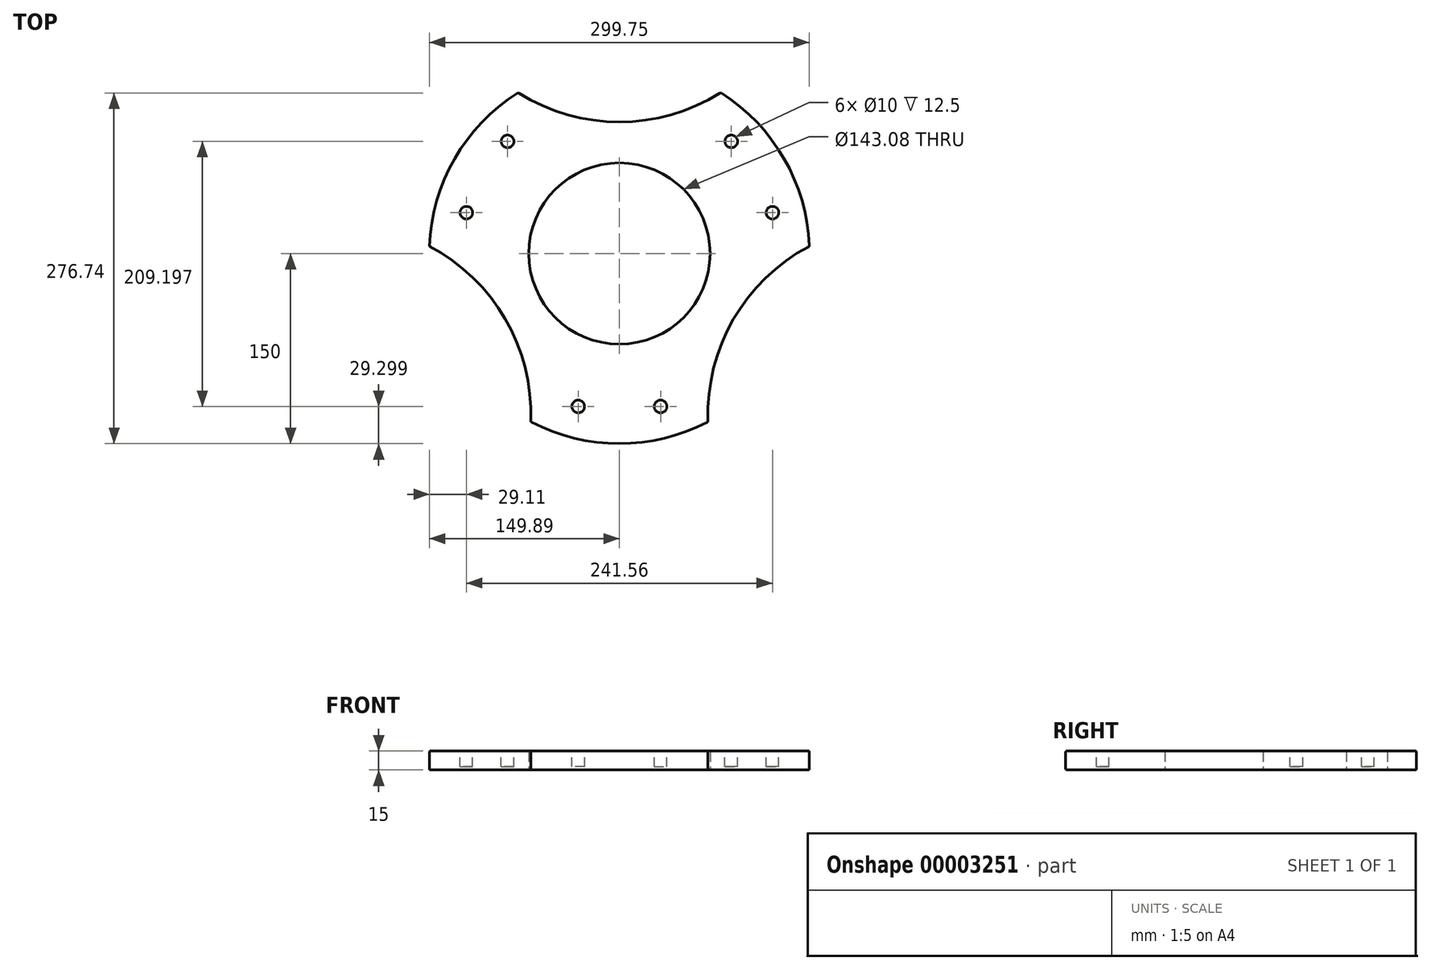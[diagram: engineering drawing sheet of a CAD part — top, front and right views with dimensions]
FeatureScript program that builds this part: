
annotation { "Feature Type Name" : "Feature", "Feature Type Description" : "" }
export const myFeature = defineFeature(function(context is Context, id is Id, definition is map)
    precondition{}
    {
        {
            var Q0;
            Q0=qCreatedBy(makeId("Top.planeOp"),FACE);
            var sketch = newSketch(context, id + "F0", { "sketchPlane" : qUnion([Q0])});
            skLineSegment(sketch, "E0", {"start": v(0, 0) * mm, "end": v(0, -150) * mm, "construction": true});
            skArc(sketch, "E1", {"start": v(-61.95, 35.77) * mm, "mid": v(-61.95, -35.77) * mm, "end": v(0, -71.54) * mm});
            skArc(sketch, "E2", {"start": v(-129.9, 75) * mm, "mid": v(-144.12, 41.6) * mm, "end": v(-149.89, 5.76) * mm});
            skLineSegment(sketch, "E3", {"start": v(0, 0) * mm, "end": v(-129.9, -75) * mm, "construction": true});
            skArc(sketch, "E4", {"start": v(-69.95, -132.69) * mm, "mid": v(-89.94, -51.93) * mm, "end": v(-149.89, 5.76) * mm});
            skLineSegment(sketch, "E5", {"start": v(0, 0) * mm, "end": v(-129.9, 75) * mm, "construction": true});
            skLineSegment(sketch, "E6", {"start": v(-129.9, 75) * mm, "end": v(-61.95, 35.77) * mm});
            skLineSegment(sketch, "E7", {"start": v(0, -71.54) * mm, "end": v(0, -150) * mm});
            skArc(sketch, "E8.trimOffspring", {"start": v(-69.95, -132.69) * mm, "mid": v(-36.03, -145.6) * mm, "end": v(0, -150) * mm});
            skSolve(sketch);
        }
        {
            var Q0;
            Q0=makeQuery(id+"F0.imprint","IMPRINT",FACE,{"disambiguationData":[TD([[makeQuery(id+"F0.imprint","IMPRINT",EDGE,{"derivedFrom":sQuery(id+"F0.wireOp",EDGE,"E1")}),-1.0]])]});
            extrude(context, id + "F1", {"entities" : qUnion([Q0]), "depth" : 15 * mm});
        }
        {
            var Q0;
            Q0=makeQuery(id+"F1.opExtrude","CAP_FACE",FACE,{"disambiguationData":[OSD([sQuery(id+"F0.wireOp",EDGE,"E1"),sQuery(id+"F0.wireOp",EDGE,"E2"),sQuery(id+"F0.wireOp",EDGE,"E4"),sQuery(id+"F0.wireOp",EDGE,"E6"),sQuery(id+"F0.wireOp",EDGE,"E7"),sQuery(id+"F0.wireOp",EDGE,"E8.trimOffspring")])],"isStart":false});
            var sketch = newSketch(context, id + "F2", { "sketchPlane" : qUnion([Q0])});
            skCircle(sketch, "E9", {"center": v(-32.5, -120.7) * mm, "radius": 5 * mm});
            skCircle(sketch, "E10", {"center": v(0, 0) * mm, "radius": 125 * mm, "construction": true});
            skLineSegment(sketch, "E11.0", {"start": v(0, 0) * mm, "end": v(-129.9, -75) * mm, "construction": true});
            skLineSegment(sketch, "E12.0", {"start": v(0, 0) * mm, "end": v(0, -150) * mm, "construction": true});
            skSolve(sketch);
        }
        {
            var Q0;
            Q0=makeQuery(id+"F2.imprint","IMPRINT",FACE,{"disambiguationData":[TD([[makeQuery(id+"F2.imprint","IMPRINT",EDGE,{"derivedFrom":sQuery(id+"F2.wireOp",EDGE,"E9")}),1.0]])]});
            extrude(context, id + "F3", {"entities" : qUnion([Q0]), "oppositeDirection" : true, "depth" : 12.5 * mm});
        }
        {
            var Q0;
            Q0=sQuery(id+"F0.wireOp",EDGE,"E3");
            cPlane(context, id + "F4", {"entities" : qUnion([Q0]), "cplaneType" : CPlaneType.LINE_ANGLE, "offset" : 150 * mm, "angle" : 0 * degree, "width" : 150 * mm, "height" : 150 * mm});
        }
        {
            var Q0;
            Q0=makeQuery(id+"F3.opExtrude","SWEPT_BODY",BODY,{"disambiguationData":[OSD([sQuery(id+"F2.wireOp",EDGE,"E9")])]});
            var Q1;
            Q1=qCreatedBy(id+"F4.planeOp",FACE);
            mirror(context, id + "F5", {"entities" : qUnion([Q0]), "mirrorPlane" : qUnion([Q1])});
        }
        {
            var Q0;
            Q0=makeQuery(id+"F3.opExtrude","SWEPT_BODY",BODY,{"disambiguationData":[OSD([sQuery(id+"F2.wireOp",EDGE,"E9")])]});
            var Q1;
            Q1=makeQuery(id+"F5.opPattern","COPY",BODY,{"derivedFrom":makeQuery(id+"F3.opExtrude","SWEPT_BODY",BODY,{"disambiguationData":[OSD([sQuery(id+"F2.wireOp",EDGE,"E9")])]}),"instanceName":"1"});
            var Q2;
            Q2=makeQuery(id+"F1.opExtrude","SWEPT_BODY",BODY,{"disambiguationData":[OSD([sQuery(id+"F0.wireOp",EDGE,"E1"),sQuery(id+"F0.wireOp",EDGE,"E2"),sQuery(id+"F0.wireOp",EDGE,"E4"),sQuery(id+"F0.wireOp",EDGE,"E6"),sQuery(id+"F0.wireOp",EDGE,"E7"),sQuery(id+"F0.wireOp",EDGE,"E8.trimOffspring")])]});
            booleanBodies(context, id + "F6", {"operationType" : BooleanOperationType.SUBTRACTION, "tools" : qUnion([Q0, Q1]), "targets" : qUnion([Q2])});
        }
        {
            var Q0;
            Q0=makeQuery(id+"F1.opExtrude","SWEPT_BODY",BODY,{"disambiguationData":[OSD([sQuery(id+"F0.wireOp",EDGE,"E1"),sQuery(id+"F0.wireOp",EDGE,"E2"),sQuery(id+"F0.wireOp",EDGE,"E4"),sQuery(id+"F0.wireOp",EDGE,"E6"),sQuery(id+"F0.wireOp",EDGE,"E7"),sQuery(id+"F0.wireOp",EDGE,"E8.trimOffspring")])]});
            var Q1;
            Q1=makeQuery(id+"F1.opExtrude","SWEPT_FACE",FACE,{"disambiguationData":[OSD([sQuery(id+"F0.wireOp",EDGE,"E1")])]});
            circularPattern(context, id + "F7", {"entities" : qUnion([Q0]), "axis" : qUnion([Q1]), "angle" : 360 * degree, "instanceCount" : 3, "equalSpace" : true});
        }
        {
            var Q0;
            Q0=makeQuery(id+"F1.opExtrude","SWEPT_BODY",BODY,{"disambiguationData":[OSD([sQuery(id+"F0.wireOp",EDGE,"E1"),sQuery(id+"F0.wireOp",EDGE,"E2"),sQuery(id+"F0.wireOp",EDGE,"E4"),sQuery(id+"F0.wireOp",EDGE,"E6"),sQuery(id+"F0.wireOp",EDGE,"E7"),sQuery(id+"F0.wireOp",EDGE,"E8.trimOffspring")])]});
            var Q1;
            Q1=makeQuery(id+"F7.opPattern","COPY",BODY,{"derivedFrom":makeQuery(id+"F1.opExtrude","SWEPT_BODY",BODY,{"disambiguationData":[OSD([sQuery(id+"F0.wireOp",EDGE,"E1"),sQuery(id+"F0.wireOp",EDGE,"E2"),sQuery(id+"F0.wireOp",EDGE,"E4"),sQuery(id+"F0.wireOp",EDGE,"E6"),sQuery(id+"F0.wireOp",EDGE,"E7"),sQuery(id+"F0.wireOp",EDGE,"E8.trimOffspring")])]}),"instanceName":"2"});
            var Q2;
            Q2=makeQuery(id+"F7.opPattern","COPY",BODY,{"derivedFrom":makeQuery(id+"F1.opExtrude","SWEPT_BODY",BODY,{"disambiguationData":[OSD([sQuery(id+"F0.wireOp",EDGE,"E1"),sQuery(id+"F0.wireOp",EDGE,"E2"),sQuery(id+"F0.wireOp",EDGE,"E4"),sQuery(id+"F0.wireOp",EDGE,"E6"),sQuery(id+"F0.wireOp",EDGE,"E7"),sQuery(id+"F0.wireOp",EDGE,"E8.trimOffspring")])]}),"instanceName":"1"});
            booleanBodies(context, id + "F8", {"operationType" : BooleanOperationType.UNION, "tools" : qUnion([Q0, Q1, Q2])});
        }
        {
            var Q0;
            Q0=makeQuery(id+"F8.opBoolean","MERGE",EDGE,{"derivedFrom":[makeQuery(id+"F1.opExtrude","CAP_EDGE",EDGE,{"disambiguationData":[OSD([sQuery(id+"F0.wireOp",EDGE,"E8.trimOffspring")])],"isStart":false}),makeQuery(id+"F7.opPattern","COPY",EDGE,{"derivedFrom":makeQuery(id+"F1.opExtrude","CAP_EDGE",EDGE,{"disambiguationData":[OSD([sQuery(id+"F0.wireOp",EDGE,"E2")])],"isStart":false}),"instanceName":"1"})]});
            var Q1;
            Q1=makeQuery(id+"F7.opPattern","COPY",EDGE,{"derivedFrom":makeQuery(id+"F1.opExtrude","SWEPT_EDGE",EDGE,{"disambiguationData":[OSD([sQuery(id+"F0.wireOp",EDGE,"E2"),sQuery(id+"F0.wireOp",EDGE,"E4")])]}),"instanceName":"1"});
            var Q2;
            Q2=makeQuery(id+"F7.opPattern","COPY",EDGE,{"derivedFrom":makeQuery(id+"F1.opExtrude","CAP_EDGE",EDGE,{"disambiguationData":[OSD([sQuery(id+"F0.wireOp",EDGE,"E4")])],"isStart":false}),"instanceName":"1"});
            var Q3;
            Q3=makeQuery(id+"F7.opPattern","COPY",EDGE,{"derivedFrom":makeQuery(id+"F1.opExtrude","SWEPT_EDGE",EDGE,{"disambiguationData":[OSD([sQuery(id+"F0.wireOp",EDGE,"E4"),sQuery(id+"F0.wireOp",EDGE,"E8.trimOffspring")])]}),"instanceName":"1"});
            var Q4;
            Q4=makeQuery(id+"F8.opBoolean","MERGE",EDGE,{"derivedFrom":[makeQuery(id+"F7.opPattern","COPY",EDGE,{"derivedFrom":makeQuery(id+"F1.opExtrude","CAP_EDGE",EDGE,{"disambiguationData":[OSD([sQuery(id+"F0.wireOp",EDGE,"E8.trimOffspring")])],"isStart":false}),"instanceName":"1"}),makeQuery(id+"F7.opPattern","COPY",EDGE,{"derivedFrom":makeQuery(id+"F1.opExtrude","CAP_EDGE",EDGE,{"disambiguationData":[OSD([sQuery(id+"F0.wireOp",EDGE,"E2")])],"isStart":false}),"instanceName":"2"})]});
            var Q5;
            Q5=makeQuery(id+"F7.opPattern","COPY",EDGE,{"derivedFrom":makeQuery(id+"F1.opExtrude","SWEPT_EDGE",EDGE,{"disambiguationData":[OSD([sQuery(id+"F0.wireOp",EDGE,"E2"),sQuery(id+"F0.wireOp",EDGE,"E4")])]}),"instanceName":"2"});
            var Q6;
            Q6=makeQuery(id+"F7.opPattern","COPY",EDGE,{"derivedFrom":makeQuery(id+"F1.opExtrude","CAP_EDGE",EDGE,{"disambiguationData":[OSD([sQuery(id+"F0.wireOp",EDGE,"E4")])],"isStart":false}),"instanceName":"2"});
            var Q7;
            Q7=makeQuery(id+"F7.opPattern","COPY",EDGE,{"derivedFrom":makeQuery(id+"F1.opExtrude","SWEPT_EDGE",EDGE,{"disambiguationData":[OSD([sQuery(id+"F0.wireOp",EDGE,"E4"),sQuery(id+"F0.wireOp",EDGE,"E8.trimOffspring")])]}),"instanceName":"2"});
            var Q8;
            Q8=makeQuery(id+"F8.opBoolean","MERGE",EDGE,{"derivedFrom":[makeQuery(id+"F1.opExtrude","CAP_EDGE",EDGE,{"disambiguationData":[OSD([sQuery(id+"F0.wireOp",EDGE,"E2")])],"isStart":false}),makeQuery(id+"F7.opPattern","COPY",EDGE,{"derivedFrom":makeQuery(id+"F1.opExtrude","CAP_EDGE",EDGE,{"disambiguationData":[OSD([sQuery(id+"F0.wireOp",EDGE,"E8.trimOffspring")])],"isStart":false}),"instanceName":"2"})]});
            var Q9;
            Q9=makeQuery(id+"F1.opExtrude","CAP_EDGE",EDGE,{"disambiguationData":[OSD([sQuery(id+"F0.wireOp",EDGE,"E4")])],"isStart":false});
            var Q10;
            Q10=makeQuery(id+"F1.opExtrude","SWEPT_EDGE",EDGE,{"disambiguationData":[OSD([sQuery(id+"F0.wireOp",EDGE,"E4"),sQuery(id+"F0.wireOp",EDGE,"E8.trimOffspring")])]});
            var Q11;
            Q11=makeQuery(id+"F8.opBoolean","MERGE",EDGE,{"derivedFrom":[makeQuery(id+"F1.opExtrude","CAP_EDGE",EDGE,{"disambiguationData":[OSD([sQuery(id+"F0.wireOp",EDGE,"E8.trimOffspring")])],"isStart":true}),makeQuery(id+"F7.opPattern","COPY",EDGE,{"derivedFrom":makeQuery(id+"F1.opExtrude","CAP_EDGE",EDGE,{"disambiguationData":[OSD([sQuery(id+"F0.wireOp",EDGE,"E2")])],"isStart":true}),"instanceName":"1"})]});
            var Q12;
            Q12=makeQuery(id+"F1.opExtrude","CAP_EDGE",EDGE,{"disambiguationData":[OSD([sQuery(id+"F0.wireOp",EDGE,"E4")])],"isStart":true});
            var Q13;
            Q13=makeQuery(id+"F7.opPattern","COPY",EDGE,{"derivedFrom":makeQuery(id+"F1.opExtrude","CAP_EDGE",EDGE,{"disambiguationData":[OSD([sQuery(id+"F0.wireOp",EDGE,"E4")])],"isStart":true}),"instanceName":"1"});
            var Q14;
            Q14=makeQuery(id+"F8.opBoolean","MERGE",EDGE,{"derivedFrom":[makeQuery(id+"F7.opPattern","COPY",EDGE,{"derivedFrom":makeQuery(id+"F1.opExtrude","CAP_EDGE",EDGE,{"disambiguationData":[OSD([sQuery(id+"F0.wireOp",EDGE,"E8.trimOffspring")])],"isStart":true}),"instanceName":"1"}),makeQuery(id+"F7.opPattern","COPY",EDGE,{"derivedFrom":makeQuery(id+"F1.opExtrude","CAP_EDGE",EDGE,{"disambiguationData":[OSD([sQuery(id+"F0.wireOp",EDGE,"E2")])],"isStart":true}),"instanceName":"2"})]});
            var Q15;
            Q15=makeQuery(id+"F7.opPattern","COPY",EDGE,{"derivedFrom":makeQuery(id+"F1.opExtrude","CAP_EDGE",EDGE,{"disambiguationData":[OSD([sQuery(id+"F0.wireOp",EDGE,"E4")])],"isStart":true}),"instanceName":"2"});
            var Q16;
            Q16=makeQuery(id+"F8.opBoolean","MERGE",EDGE,{"derivedFrom":[makeQuery(id+"F1.opExtrude","CAP_EDGE",EDGE,{"disambiguationData":[OSD([sQuery(id+"F0.wireOp",EDGE,"E2")])],"isStart":true}),makeQuery(id+"F7.opPattern","COPY",EDGE,{"derivedFrom":makeQuery(id+"F1.opExtrude","CAP_EDGE",EDGE,{"disambiguationData":[OSD([sQuery(id+"F0.wireOp",EDGE,"E8.trimOffspring")])],"isStart":true}),"instanceName":"2"})]});
            var Q17;
            {var subQ0=makeQuery(id+"F1.opExtrude","CAP_EDGE",EDGE,{"disambiguationData":[OSD([sQuery(id+"F0.wireOp",EDGE,"E1")])],"isStart":true});Q17=makeQuery(id+"F8.opBoolean","MERGE",EDGE,{"derivedFrom":[subQ0,makeQuery(id+"F7.opPattern","COPY",EDGE,{"derivedFrom":subQ0,"instanceName":"1"}),makeQuery(id+"F7.opPattern","COPY",EDGE,{"derivedFrom":subQ0,"instanceName":"2"})]});}
            var Q18;
            {var subQ0=makeQuery(id+"F1.opExtrude","CAP_EDGE",EDGE,{"disambiguationData":[OSD([sQuery(id+"F0.wireOp",EDGE,"E1")])],"isStart":false});Q18=makeQuery(id+"F8.opBoolean","MERGE",EDGE,{"derivedFrom":[subQ0,makeQuery(id+"F7.opPattern","COPY",EDGE,{"derivedFrom":subQ0,"instanceName":"1"}),makeQuery(id+"F7.opPattern","COPY",EDGE,{"derivedFrom":subQ0,"instanceName":"2"})]});}
            fillet(context, id + "F9", {"entities" : qUnion([Q0, Q1, Q2, Q3, Q4, Q5, Q6, Q7, Q8, Q9, Q10, Q11, Q12, Q13, Q14, Q15, Q16, Q17, Q18]), "radius" : 1 * mm, "tangentPropagation" : true, "allowEdgeOverflow" : false});
        }
    });
